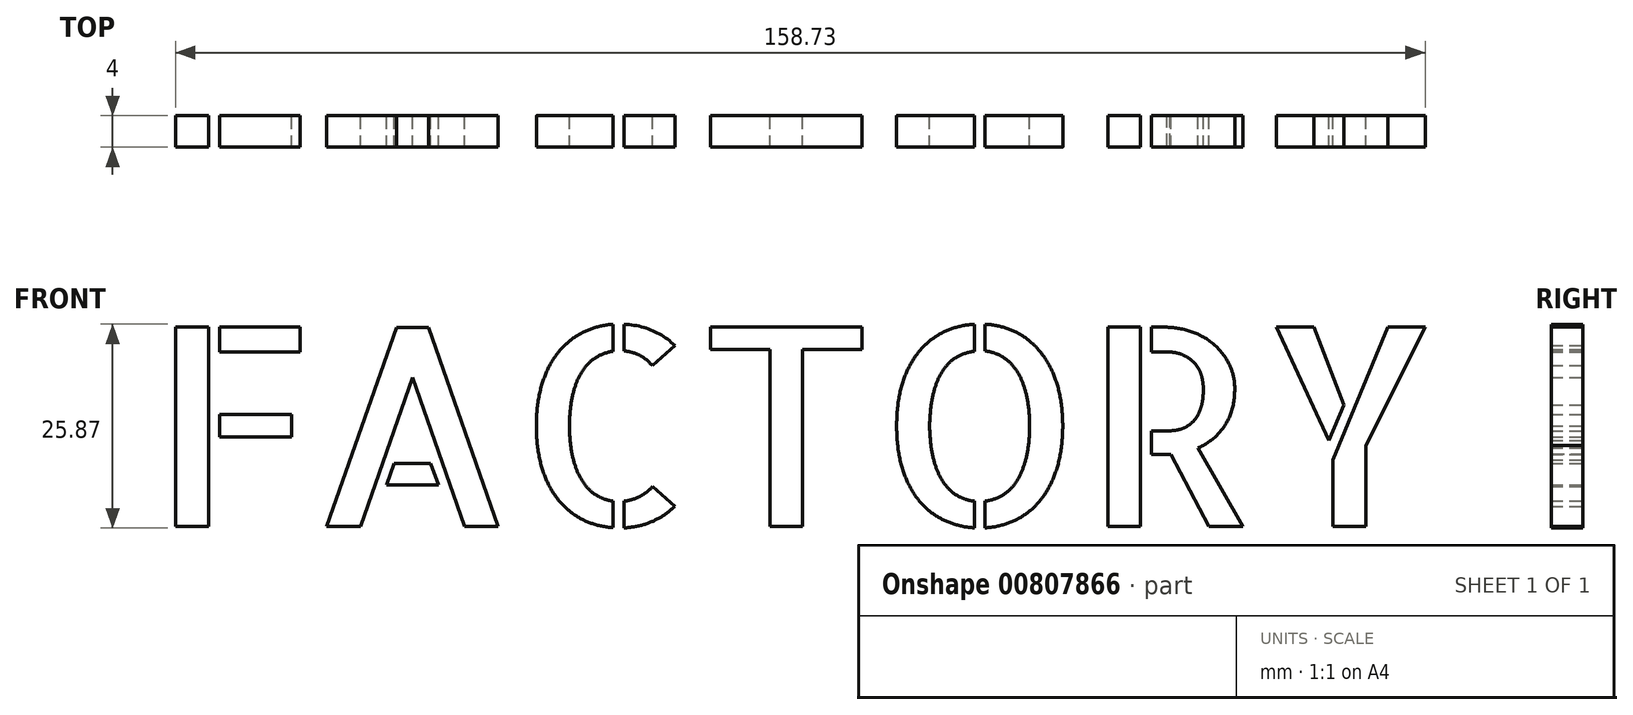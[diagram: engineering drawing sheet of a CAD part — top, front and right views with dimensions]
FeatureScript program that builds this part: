
annotation { "Feature Type Name" : "Feature", "Feature Type Description" : "" }
export const myFeature = defineFeature(function(context is Context, id is Id, definition is map)
    precondition{}
    {
        {
            var Q0;
            Q0=qCreatedBy(makeId("Front.planeOp"),FACE);
            var sketch = newSketch(context, id + "F0", { "sketchPlane" : qUnion([Q0])});
            skText(sketch, "E0", { "text": "FACTORY", "fontName": "AllertaStencil-Regular.ttf"});
            const initialGuessF0  = {"E0": [0, -0.02533, 1, 0, 0.02533]};
            skSetInitialGuess(sketch, initialGuessF0);
            skSolve(sketch);
        }
        {
            var Q0;
            Q0 = qSketchRegion(id + "F0", true);
            extrude(context, id + "F1", {"entities" : qUnion([Q0]), "depth" : 4 * mm, "offsetDistance" : 25 * mm});
        }
    });
